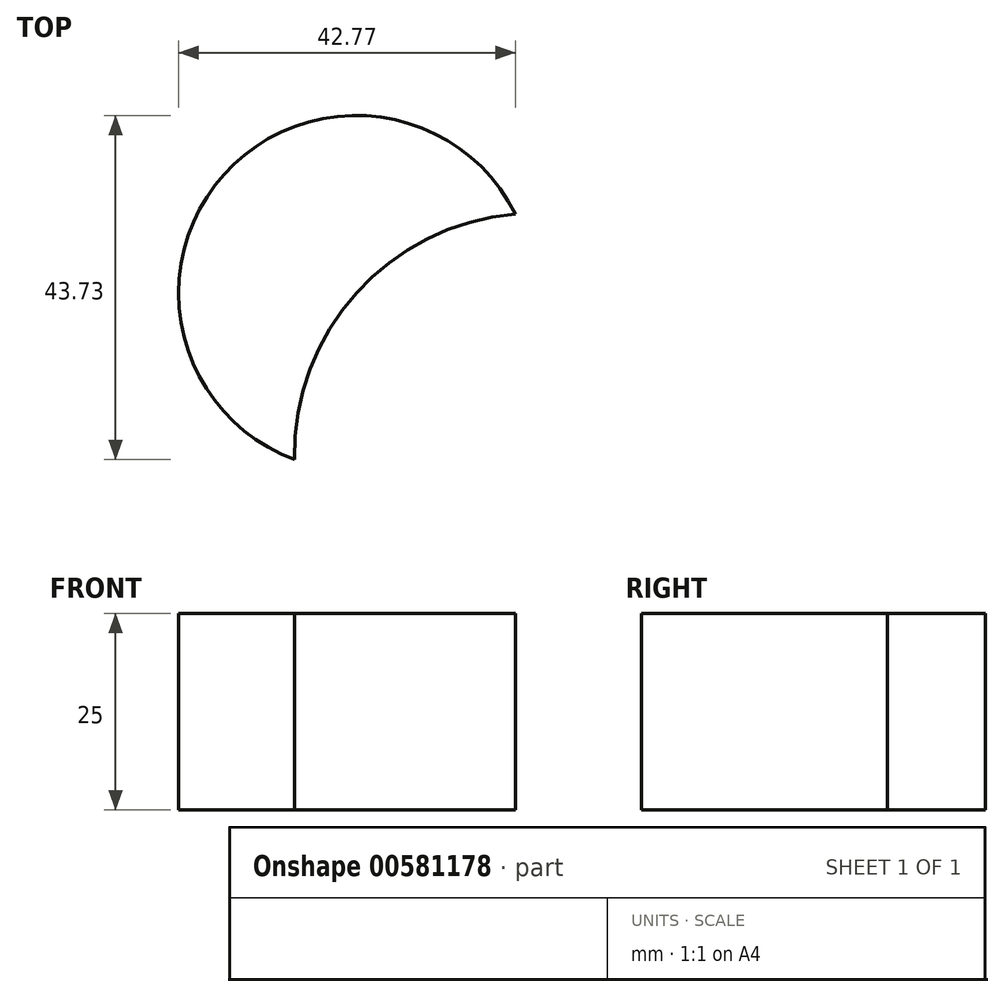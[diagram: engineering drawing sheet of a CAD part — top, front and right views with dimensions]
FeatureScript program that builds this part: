
annotation { "Feature Type Name" : "Feature", "Feature Type Description" : "" }
export const myFeature = defineFeature(function(context is Context, id is Id, definition is map)
    precondition{}
    {
        {
            var Q0;
            Q0=qCreatedBy(makeId("Top.planeOp"),FACE);
            var sketch = newSketch(context, id + "F0", { "sketchPlane" : qUnion([Q0])});
            skCircle(sketch, "E0", {"center": v(0, 0) * mm, "radius": 30.7 * mm});
            skCircle(sketch, "E1", {"center": v(-22.85, 20.52) * mm, "radius": 22.57 * mm});
            skSolve(sketch);
        }
        {
            var Q0;
            {var subQ0=sQuery(id+"F0.wireOp",EDGE,"E1");var subQ1=sQuery(id+"F0.wireOp",EDGE,"E0");var subQ2=makeQuery(id+"F0.imprint","INTERSECT",VERTEX,{"disambiguationData":[OD(0.0)],"derivedFrom":[subQ1,subQ0]});Q0=makeQuery(id+"F0.imprint","IMPRINT",FACE,{"disambiguationData":[TD([[makeQuery(id+"F0.imprint","IMPRINT",EDGE,{"disambiguationData":[TD([[subQ2,1.0]])],"derivedFrom":subQ1}),-1.0]])]});}
            extrude(context, id + "F1", {"entities" : qUnion([Q0]), "depth" : 25 * mm, "offsetDistance" : 25 * mm});
        }
    });
